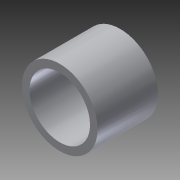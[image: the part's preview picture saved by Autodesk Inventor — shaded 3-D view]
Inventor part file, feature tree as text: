
AUTODESK INVENTOR PART (.ipt)
format: ipt  version: 2013 (Build 170138000, 138)  size: 82,944 bytes
history: native  units: in
note: dims shown in document units (in); Inventor stores cm internally (conversion verified against a paired STEP export)
features: extrude x1, sketch x1
ambient origin geometry x8: Origin, YZ Plane, XZ Plane, XY Plane, X Axis, Y Axis, Z Axis, Center Point
bodies: Solid1 (feature_tree)
feature tree (2):
  extrude  "Extrusion1"  Depth=0.625in
  sketch  "Sketch1"  dims[d0=0.5in d1=0.625in d2=0.5in d3=0.0in]
